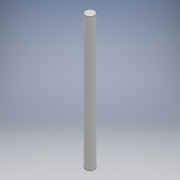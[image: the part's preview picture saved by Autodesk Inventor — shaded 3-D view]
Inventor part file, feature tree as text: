
AUTODESK INVENTOR PART (.ipt)
format: ipt  version: 2018 (Build 220112000, 112)  size: 89,600 bytes
history: native  units: mm
features: extrude x1, sketch x1
ambient origin geometry x8: Origin, YZ Plane, XZ Plane, XY Plane, X Axis, Y Axis, Z Axis, Center Point
bodies: Solid1 (feature_tree)
feature tree (2):
  extrude  "Extrusion1"  Depth=1500.0mm TaperAngle=0.0deg
  sketch  "Sketch1"  dims[d0=100.0mm d1=1500.0mm d2=0.0mm]
